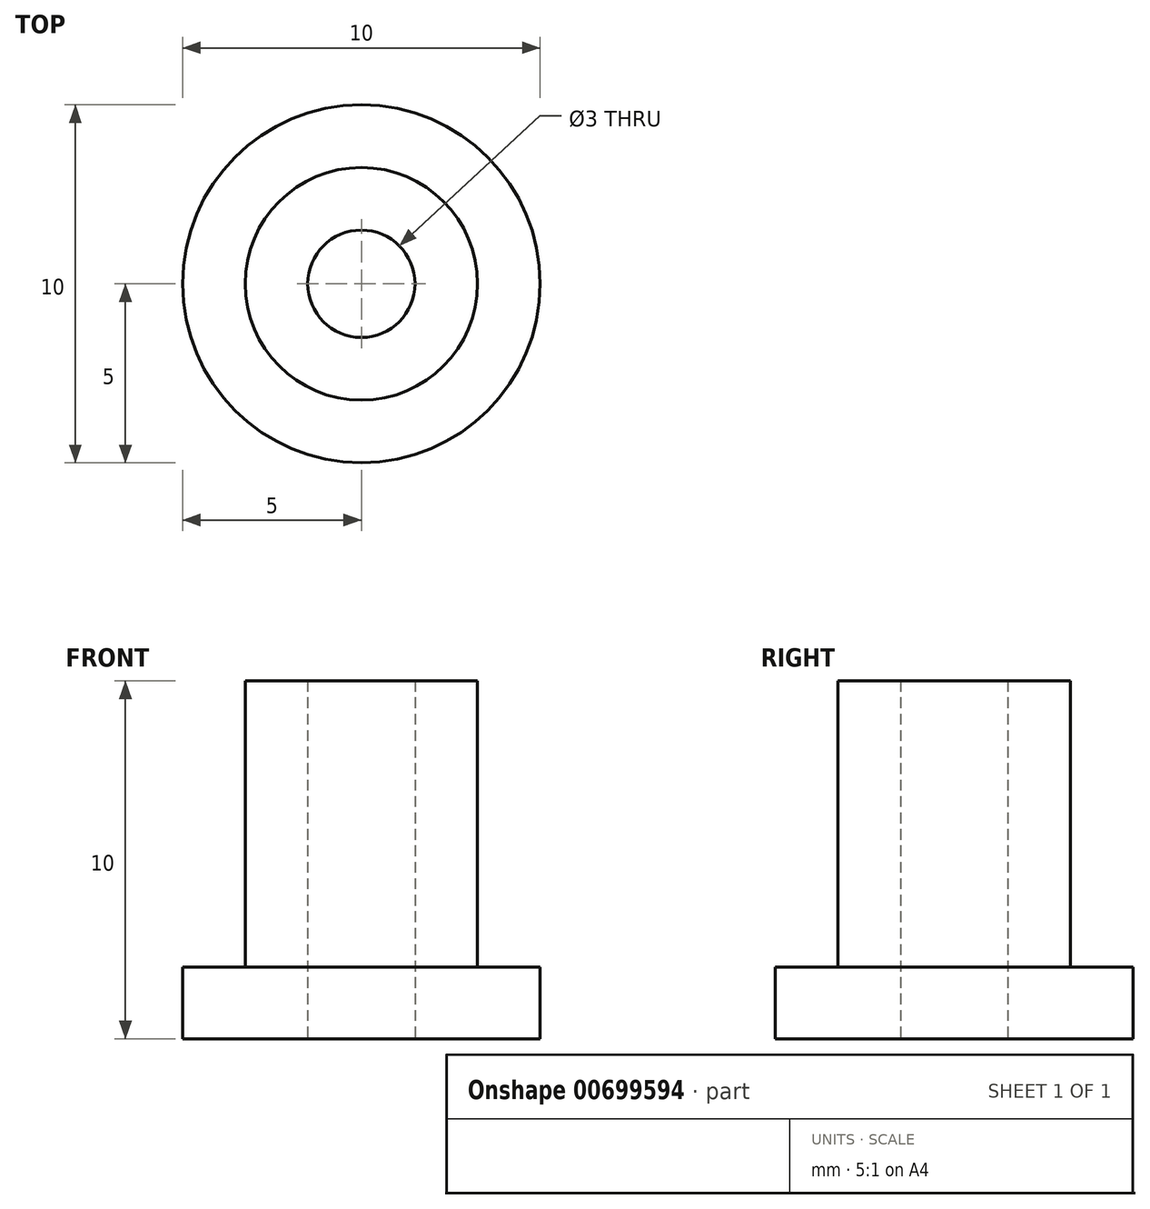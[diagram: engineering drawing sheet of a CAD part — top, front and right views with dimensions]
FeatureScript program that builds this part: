
annotation { "Feature Type Name" : "Feature", "Feature Type Description" : "" }
export const myFeature = defineFeature(function(context is Context, id is Id, definition is map)
    precondition{}
    {
        {
            var Q0;
            Q0=qCreatedBy(makeId("Top.planeOp"),FACE);
            var sketch = newSketch(context, id + "F0", { "sketchPlane" : qUnion([Q0])});
            skCircle(sketch, "E0", {"center": v(0, 0) * mm, "radius": 3.25 * mm});
            skCircle(sketch, "E1", {"center": v(0, 0) * mm, "radius": 1.5 * mm});
            skSolve(sketch);
        }
        {
            var Q0;
            Q0=makeQuery(id+"F0.imprint","IMPRINT",FACE,{"disambiguationData":[TD([[makeQuery(id+"F0.imprint","IMPRINT",EDGE,{"derivedFrom":sQuery(id+"F0.wireOp",EDGE,"E0")}),1.0]])]});
            extrude(context, id + "F1", {"entities" : qUnion([Q0]), "depth" : 10 * mm, "offsetDistance" : 25 * mm});
        }
        {
            var Q0;
            Q0=qCreatedBy(makeId("Top.planeOp"),FACE);
            var sketch = newSketch(context, id + "F2", { "sketchPlane" : qUnion([Q0])});
            skCircle(sketch, "E2", {"center": v(0, 0) * mm, "radius": 5 * mm});
            skSolve(sketch);
        }
        {
            var Q0;
            Q0=makeQuery(id+"F2.imprint","IMPRINT",FACE,{"disambiguationData":[TD([[makeQuery(id+"F2.imprint","IMPRINT",EDGE,{"derivedFrom":sQuery(id+"F2.wireOp",EDGE,"E2")}),1.0]])]});
            extrude(context, id + "F3", {"entities" : qUnion([Q0]), "operationType" : NewBodyOperationType.ADD, "depth" : 2 * mm, "offsetDistance" : 25 * mm});
        }
        {
            var Q0;
            Q0=makeQuery(id+"F3.boolean.opBoolean","SPLIT",FACE,{"disambiguationData":[TD([makeQuery(id+"F1.opExtrude","SWEPT_FACE",FACE,{"disambiguationData":[OSD([sQuery(id+"F0.wireOp",EDGE,"E1")])]})])],"derivedFrom":makeQuery(id+"F3.opExtrude","CAP_FACE",FACE,{"disambiguationData":[OSD([sQuery(id+"F2.wireOp",EDGE,"E2")])],"isStart":false})});
            extrude(context, id + "F4", {"entities" : qUnion([Q0]), "operationType" : NewBodyOperationType.REMOVE, "oppositeDirection" : true, "depth" : 25 * mm, "offsetDistance" : 25 * mm});
        }
    });
